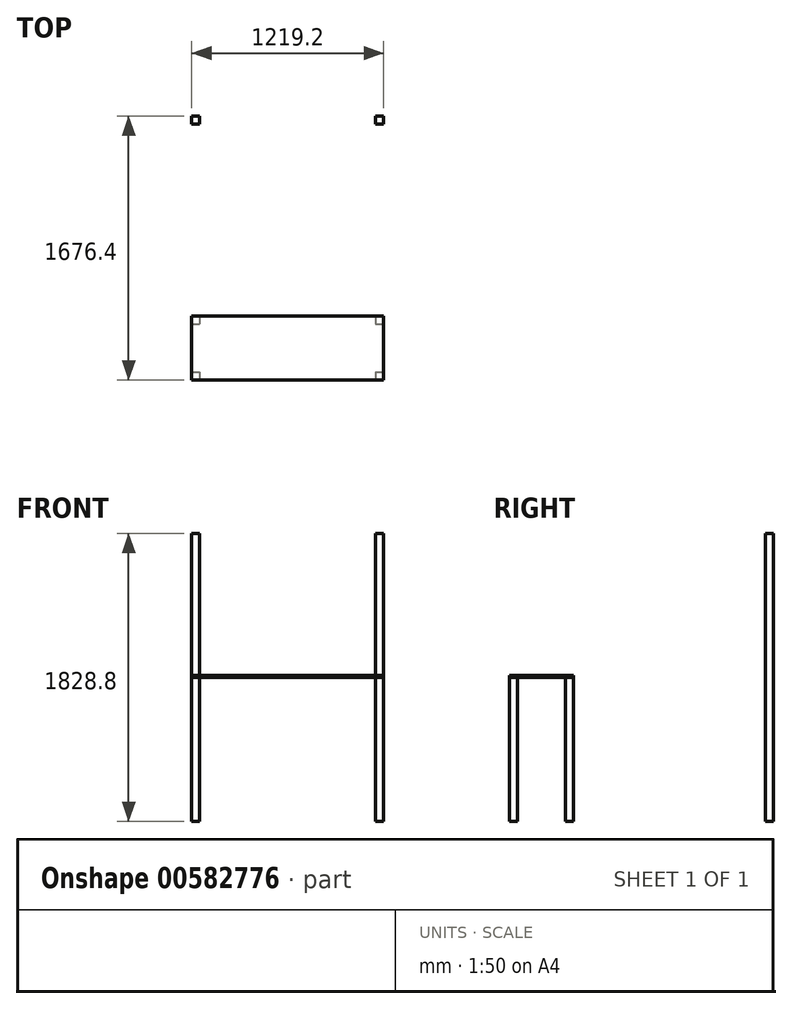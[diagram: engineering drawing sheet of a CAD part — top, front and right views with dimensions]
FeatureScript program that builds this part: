
annotation { "Feature Type Name" : "Feature", "Feature Type Description" : "" }
export const myFeature = defineFeature(function(context is Context, id is Id, definition is map)
    precondition{}
    {
        {
            var Q0;
            Q0=qCreatedBy(makeId("Top.planeOp"),FACE);
            var sketch = newSketch(context, id + "F0", { "sketchPlane" : qUnion([Q0])});
            skLineSegment(sketch, "E0.bottom", {"start": v(-169.27, 112.97) * mm, "end": v(-118.47, 112.97) * mm});
            skLineSegment(sketch, "E0.top", {"start": v(-169.27, 62.17) * mm, "end": v(-118.47, 62.17) * mm});
            skLineSegment(sketch, "E0.left", {"start": v(-169.27, 112.97) * mm, "end": v(-169.27, 62.17) * mm});
            skLineSegment(sketch, "E0.right", {"start": v(-118.47, 112.97) * mm, "end": v(-118.47, 62.17) * mm});
            skLineSegment(sketch, "E1.bottom", {"start": v(999.13, 112.97) * mm, "end": v(1049.93, 112.97) * mm});
            skLineSegment(sketch, "E1.top", {"start": v(999.13, 62.17) * mm, "end": v(1049.93, 62.17) * mm});
            skLineSegment(sketch, "E1.left", {"start": v(999.13, 112.97) * mm, "end": v(999.13, 62.17) * mm});
            skLineSegment(sketch, "E1.right", {"start": v(1049.93, 112.97) * mm, "end": v(1049.93, 62.17) * mm});
            skLineSegment(sketch, "E2.bottom", {"start": v(-169.27, -242.63) * mm, "end": v(-118.47, -242.63) * mm});
            skLineSegment(sketch, "E2.top", {"start": v(-169.27, -293.43) * mm, "end": v(-118.47, -293.43) * mm});
            skLineSegment(sketch, "E2.left", {"start": v(-169.27, -242.63) * mm, "end": v(-169.27, -293.43) * mm});
            skLineSegment(sketch, "E2.right", {"start": v(-118.47, -242.63) * mm, "end": v(-118.47, -293.43) * mm});
            skLineSegment(sketch, "E3.bottom", {"start": v(999.13, -242.63) * mm, "end": v(1049.93, -242.63) * mm});
            skLineSegment(sketch, "E3.top", {"start": v(999.13, -293.43) * mm, "end": v(1049.93, -293.43) * mm});
            skLineSegment(sketch, "E3.left", {"start": v(999.13, -242.63) * mm, "end": v(999.13, -293.43) * mm});
            skLineSegment(sketch, "E3.right", {"start": v(1049.93, -242.63) * mm, "end": v(1049.93, -293.43) * mm});
            skLineSegment(sketch, "E4.bottom", {"start": v(-169.27, 1382.97) * mm, "end": v(-118.47, 1382.97) * mm});
            skLineSegment(sketch, "E4.top", {"start": v(-169.27, 1332.17) * mm, "end": v(-118.47, 1332.17) * mm});
            skLineSegment(sketch, "E4.left", {"start": v(-169.27, 1382.97) * mm, "end": v(-169.27, 1332.17) * mm});
            skLineSegment(sketch, "E4.right", {"start": v(-118.47, 1382.97) * mm, "end": v(-118.47, 1332.17) * mm});
            skLineSegment(sketch, "E5.bottom", {"start": v(999.13, 1382.97) * mm, "end": v(1049.93, 1382.97) * mm});
            skLineSegment(sketch, "E5.top", {"start": v(999.13, 1332.17) * mm, "end": v(1049.93, 1332.17) * mm});
            skLineSegment(sketch, "E5.left", {"start": v(999.13, 1382.97) * mm, "end": v(999.13, 1332.17) * mm});
            skLineSegment(sketch, "E5.right", {"start": v(1049.93, 1382.97) * mm, "end": v(1049.93, 1332.17) * mm});
            skLineSegment(sketch, "E6", {"start": v(-118.47, 62.17) * mm, "end": v(999.13, 62.17) * mm, "construction": true});
            skLineSegment(sketch, "E7", {"start": v(999.13, 62.17) * mm, "end": v(999.13, -242.63) * mm, "construction": true});
            skLineSegment(sketch, "E8", {"start": v(999.13, -242.63) * mm, "end": v(-118.47, -242.63) * mm, "construction": true});
            skLineSegment(sketch, "E9", {"start": v(-118.47, -242.63) * mm, "end": v(-118.47, 62.17) * mm, "construction": true});
            skLineSegment(sketch, "E10", {"start": v(-118.47, 1332.17) * mm, "end": v(-118.47, 112.97) * mm, "construction": true});
            skLineSegment(sketch, "E11", {"start": v(-118.47, 112.97) * mm, "end": v(999.13, 112.97) * mm, "construction": true});
            skLineSegment(sketch, "E12", {"start": v(999.13, 112.97) * mm, "end": v(999.13, 1332.17) * mm, "construction": true});
            skLineSegment(sketch, "E13", {"start": v(999.13, 1332.17) * mm, "end": v(-118.47, 1332.17) * mm, "construction": true});
            skSolve(sketch);
        }
        {
            var Q0;
            Q0=makeQuery(id+"F0.imprint","IMPRINT",FACE,{"disambiguationData":[TD([[makeQuery(id+"F0.imprint","IMPRINT",EDGE,{"derivedFrom":sQuery(id+"F0.wireOp",EDGE,"E0.bottom")}),-1.0]])]});
            var Q1;
            Q1=makeQuery(id+"F0.imprint","IMPRINT",FACE,{"disambiguationData":[TD([[makeQuery(id+"F0.imprint","IMPRINT",EDGE,{"derivedFrom":sQuery(id+"F0.wireOp",EDGE,"E1.bottom")}),-1.0]])]});
            var Q2;
            Q2=makeQuery(id+"F0.imprint","IMPRINT",FACE,{"disambiguationData":[TD([[makeQuery(id+"F0.imprint","IMPRINT",EDGE,{"derivedFrom":sQuery(id+"F0.wireOp",EDGE,"E2.bottom")}),-1.0]])]});
            var Q3;
            Q3=makeQuery(id+"F0.imprint","IMPRINT",FACE,{"disambiguationData":[TD([[makeQuery(id+"F0.imprint","IMPRINT",EDGE,{"derivedFrom":sQuery(id+"F0.wireOp",EDGE,"E3.bottom")}),-1.0]])]});
            extrude(context, id + "F1", {"entities" : qUnion([Q0, Q1, Q2, Q3]), "depth" : 914.4 * mm, "offsetDistance" : 25.4 * mm});
        }
        {
            var Q0;
            Q0=makeQuery(id+"F1.opExtrude","CAP_FACE",FACE,{"disambiguationData":[OSD([sQuery(id+"F0.wireOp",EDGE,"E0.bottom"),sQuery(id+"F0.wireOp",EDGE,"E0.top"),sQuery(id+"F0.wireOp",EDGE,"E0.left"),sQuery(id+"F0.wireOp",EDGE,"E0.right")])],"isStart":false});
            var sketch = newSketch(context, id + "F2", { "sketchPlane" : qUnion([Q0])});
            skLineSegment(sketch, "E14.bottom", {"start": v(-169.27, 112.97) * mm, "end": v(1049.93, 112.97) * mm});
            skLineSegment(sketch, "E14.top", {"start": v(-169.27, -293.43) * mm, "end": v(1049.93, -293.43) * mm});
            skLineSegment(sketch, "E14.left", {"start": v(-169.27, 112.97) * mm, "end": v(-169.27, -293.43) * mm});
            skLineSegment(sketch, "E14.right", {"start": v(1049.93, 112.97) * mm, "end": v(1049.93, -293.43) * mm});
            skSolve(sketch);
        }
        {
            var Q0;
            Q0 = qSketchRegion(id + "F2", true);
            extrude(context, id + "F3", {"entities" : qUnion([Q0]), "depth" : 12.7 * mm, "offsetDistance" : 25.4 * mm});
        }
        {
            var Q0;
            Q0=makeQuery(id+"F0.imprint","IMPRINT",FACE,{"disambiguationData":[TD([[makeQuery(id+"F0.imprint","IMPRINT",EDGE,{"derivedFrom":sQuery(id+"F0.wireOp",EDGE,"E4.bottom")}),-1.0]])]});
            var Q1;
            Q1=makeQuery(id+"F0.imprint","IMPRINT",FACE,{"disambiguationData":[TD([[makeQuery(id+"F0.imprint","IMPRINT",EDGE,{"derivedFrom":sQuery(id+"F0.wireOp",EDGE,"E5.bottom")}),-1.0]])]});
            extrude(context, id + "F4", {"entities" : qUnion([Q0, Q1]), "depth" : 1828.8 * mm, "offsetDistance" : 25.4 * mm});
        }
    });
